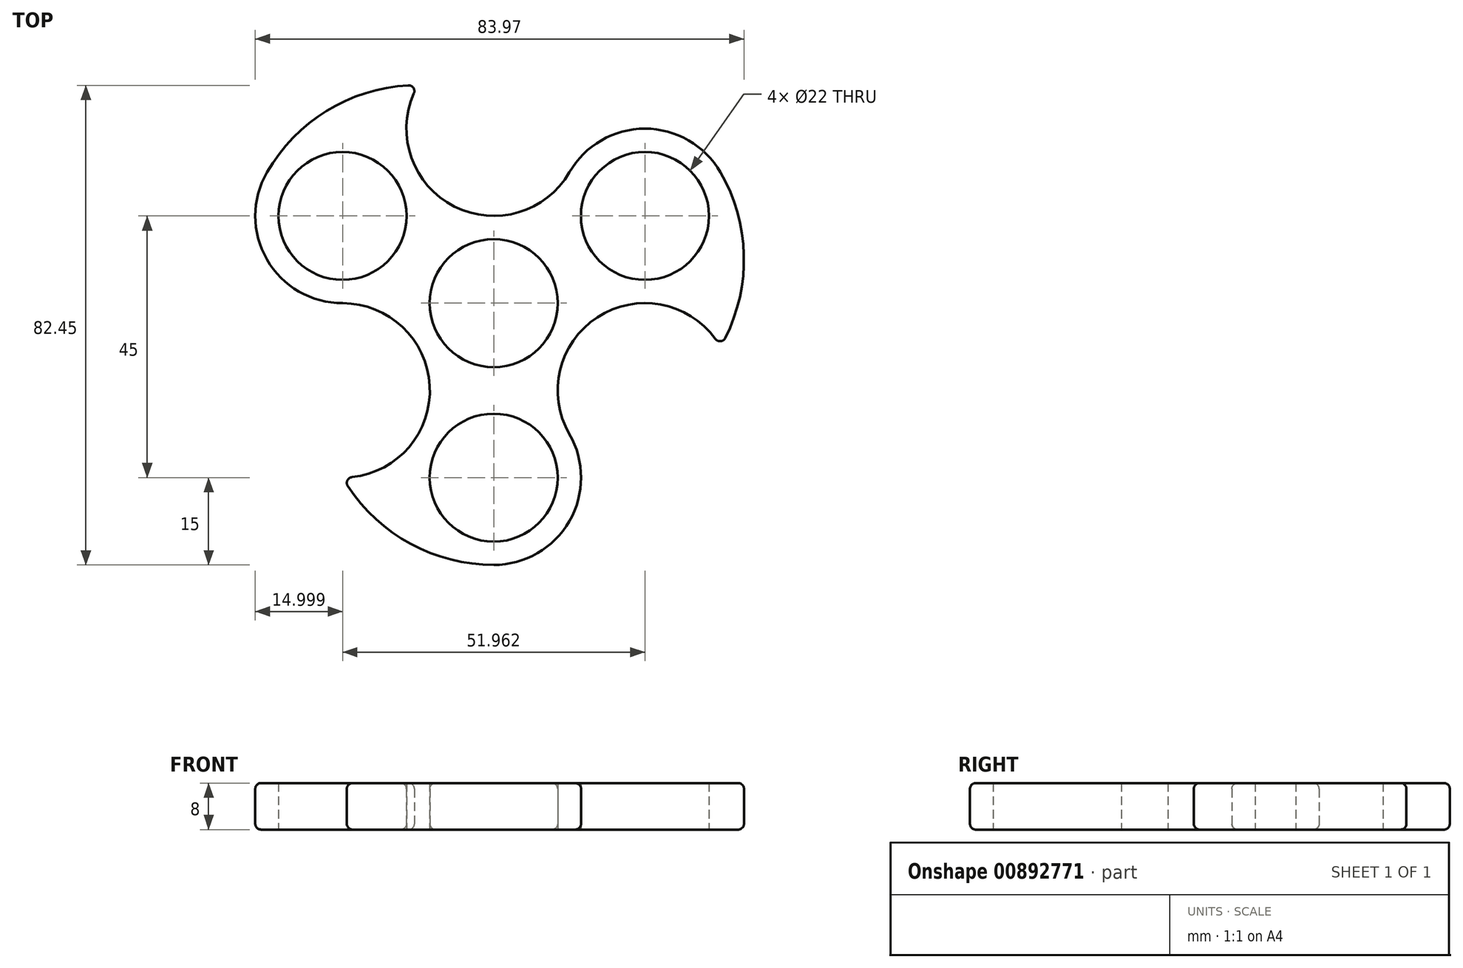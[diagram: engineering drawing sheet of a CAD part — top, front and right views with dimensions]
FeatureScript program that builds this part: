
annotation { "Feature Type Name" : "Feature", "Feature Type Description" : "" }
export const myFeature = defineFeature(function(context is Context, id is Id, definition is map)
    precondition{}
    {
        {
            var Q0;
            Q0=qCreatedBy(makeId("Top.planeOp"),FACE);
            var sketch = newSketch(context, id + "F0", { "sketchPlane" : qUnion([Q0])});
            skCircle(sketch, "E0", {"center": v(0, 0) * mm, "radius": 15 * mm});
            skCircle(sketch, "E1", {"center": v(-25.98, 15) * mm, "radius": 15 * mm});
            skCircle(sketch, "E2", {"center": v(0, -30) * mm, "radius": 15 * mm});
            skCircle(sketch, "E3", {"center": v(25.98, 15) * mm, "radius": 15 * mm});
            skLineSegment(sketch, "E4", {"start": v(-25.98, 15) * mm, "end": v(0, -30) * mm, "construction": true});
            skLineSegment(sketch, "E5", {"start": v(0, -30) * mm, "end": v(25.98, 15) * mm, "construction": true});
            skLineSegment(sketch, "E6", {"start": v(-25.98, 15) * mm, "end": v(25.98, 15) * mm, "construction": true});
            skArc(sketch, "E7", {"start": v(-13, -7.5) * mm, "mid": v(-18.48, -2) * mm, "end": v(-25.98, 0) * mm});
            skArc(sketch, "E8", {"start": v(-13, 22.5) * mm, "mid": v(-7.5, 17) * mm, "end": v(0, 15) * mm});
            skArc(sketch, "E9", {"start": v(25.98, 0) * mm, "mid": v(18.48, -2) * mm, "end": v(13, -7.5) * mm});
            skArc(sketch, "E10", {"start": v(0, 15) * mm, "mid": v(7.5, 17) * mm, "end": v(13, 22.5) * mm});
            skArc(sketch, "E11", {"start": v(-13, -22.5) * mm, "mid": v(-10.98, -15) * mm, "end": v(-13, -7.5) * mm});
            skArc(sketch, "E12", {"start": v(13, -7.5) * mm, "mid": v(10.98, -15) * mm, "end": v(13, -22.5) * mm});
            skArc(sketch, "E13", {"start": v(-25.08, -31.45) * mm, "mid": v(-14.25, -41.4) * mm, "end": v(0, -45) * mm});
            skArc(sketch, "E14", {"start": v(-24.36, -29.91) * mm, "mid": v(-17.79, -27.56) * mm, "end": v(-13, -22.5) * mm});
            skPoint(sketch, "E15.visualSharp", {"position": v(-25.98, -30) * mm});
            skArc(sketch, "E15.filletArc", {"start": v(-24.36, -29.91) * mm, "mid": v(-25.15, -30.48) * mm, "end": v(-25.08, -31.45) * mm});
            skArc(sketch, "E16.1.0", {"start": v(39.78, -6) * mm, "mid": v(42.98, 8.35) * mm, "end": v(38.97, 22.5) * mm});
            skArc(sketch, "E16.1.1", {"start": v(38.08, -6.14) * mm, "mid": v(32.77, -1.62) * mm, "end": v(25.98, 0) * mm});
            skArc(sketch, "E16.1.2", {"start": v(38.08, -6.14) * mm, "mid": v(38.97, -6.54) * mm, "end": v(39.78, -6) * mm});
            skArc(sketch, "E16.2.0", {"start": v(-14.7, 37.45) * mm, "mid": v(-28.72, 33.04) * mm, "end": v(-38.97, 22.5) * mm});
            skArc(sketch, "E16.2.1", {"start": v(-13.73, 36.05) * mm, "mid": v(-14.98, 29.19) * mm, "end": v(-13, 22.5) * mm});
            skArc(sketch, "E16.2.2", {"start": v(-13.73, 36.05) * mm, "mid": v(-13.82, 37.02) * mm, "end": v(-14.7, 37.45) * mm});
            skSolve(sketch);
        }
        {
            var Q0;
            {var subQ2=sQuery(id+"F0.wireOp",EDGE,"E16.2.0");Q0=makeQuery(id+"F0.imprint","IMPRINT",FACE,{"disambiguationData":[TD([[makeQuery(id+"F0.imprint","IMPRINT",EDGE,{"derivedFrom":subQ2}),1.0]])]});}
            var Q1;
            {var subQ0=sQuery(id+"F0.wireOp",EDGE,"E11");Q1=makeQuery(id+"F0.imprint","IMPRINT",FACE,{"disambiguationData":[TD([[makeQuery(id+"F0.imprint","IMPRINT",EDGE,{"derivedFrom":subQ0}),-1.0]])]});}
            var Q2;
            {var subQ2=sQuery(id+"F0.wireOp",EDGE,"E13");Q2=makeQuery(id+"F0.imprint","IMPRINT",FACE,{"disambiguationData":[TD([[makeQuery(id+"F0.imprint","IMPRINT",EDGE,{"derivedFrom":subQ2}),1.0]])]});}
            var Q3;
            {var subQ0=sQuery(id+"F0.wireOp",EDGE,"E12");Q3=makeQuery(id+"F0.imprint","IMPRINT",FACE,{"disambiguationData":[TD([[makeQuery(id+"F0.imprint","IMPRINT",EDGE,{"derivedFrom":subQ0}),-1.0]])]});}
            var Q4;
            {var subQ0=sQuery(id+"F0.wireOp",EDGE,"E7");Q4=makeQuery(id+"F0.imprint","IMPRINT",FACE,{"disambiguationData":[TD([[makeQuery(id+"F0.imprint","IMPRINT",EDGE,{"derivedFrom":subQ0}),-1.0]])]});}
            var Q5;
            {var subQ0=sQuery(id+"F0.wireOp",EDGE,"E0");var subQ5=makeQuery(id+"F0.imprint","INTERSECT",VERTEX,{"derivedFrom":[subQ0,sQuery(id+"F0.wireOp",EDGE,"E3")]});Q5=makeQuery(id+"F0.imprint","IMPRINT",FACE,{"disambiguationData":[TD([[makeQuery(id+"F0.imprint","IMPRINT",EDGE,{"disambiguationData":[TD([[subQ5,-1.0]])],"derivedFrom":subQ0}),1.0]])]});}
            var Q6;
            {var subQ0=sQuery(id+"F0.wireOp",EDGE,"E8");Q6=makeQuery(id+"F0.imprint","IMPRINT",FACE,{"disambiguationData":[TD([[makeQuery(id+"F0.imprint","IMPRINT",EDGE,{"derivedFrom":subQ0}),-1.0]])]});}
            var Q7;
            {var subQ0=sQuery(id+"F0.wireOp",EDGE,"E10");Q7=makeQuery(id+"F0.imprint","IMPRINT",FACE,{"disambiguationData":[TD([[makeQuery(id+"F0.imprint","IMPRINT",EDGE,{"derivedFrom":subQ0}),-1.0]])]});}
            var Q8;
            {var subQ0=sQuery(id+"F0.wireOp",EDGE,"E1");var subQ3=makeQuery(id+"F0.imprint","INTERSECT",VERTEX,{"derivedFrom":[subQ0,sQuery(id+"F0.wireOp",EDGE,"E7")]});Q8=makeQuery(id+"F0.imprint","IMPRINT",FACE,{"disambiguationData":[TD([[makeQuery(id+"F0.imprint","IMPRINT",EDGE,{"disambiguationData":[TD([[subQ3,1.0]])],"derivedFrom":subQ0}),1.0]])]});}
            var Q9;
            {var subQ2=sQuery(id+"F0.wireOp",EDGE,"E16.1.0");Q9=makeQuery(id+"F0.imprint","IMPRINT",FACE,{"disambiguationData":[TD([[makeQuery(id+"F0.imprint","IMPRINT",EDGE,{"derivedFrom":subQ2}),1.0]])]});}
            var Q10;
            {var subQ0=sQuery(id+"F0.wireOp",EDGE,"E3");var subQ1=makeQuery(id+"F0.imprint","INTERSECT",VERTEX,{"derivedFrom":[subQ0,sQuery(id+"F0.wireOp",EDGE,"E10")]});Q10=makeQuery(id+"F0.imprint","IMPRINT",FACE,{"disambiguationData":[TD([[makeQuery(id+"F0.imprint","IMPRINT",EDGE,{"disambiguationData":[TD([[subQ1,1.0]])],"derivedFrom":subQ0}),1.0]])]});}
            var Q11;
            {var subQ0=sQuery(id+"F0.wireOp",EDGE,"E2");var subQ1=makeQuery(id+"F0.imprint","INTERSECT",VERTEX,{"derivedFrom":[subQ0,sQuery(id+"F0.wireOp",EDGE,"E12")]});Q11=makeQuery(id+"F0.imprint","IMPRINT",FACE,{"disambiguationData":[TD([[makeQuery(id+"F0.imprint","IMPRINT",EDGE,{"disambiguationData":[TD([[subQ1,-1.0]])],"derivedFrom":subQ0}),1.0]])]});}
            var Q12;
            {var subQ0=sQuery(id+"F0.wireOp",EDGE,"E9");Q12=makeQuery(id+"F0.imprint","IMPRINT",FACE,{"disambiguationData":[TD([[makeQuery(id+"F0.imprint","IMPRINT",EDGE,{"derivedFrom":subQ0}),-1.0]])]});}
            extrude(context, id + "F1", {"entities" : qUnion([Q0, Q1, Q2, Q3, Q4, Q5, Q6, Q7, Q8, Q9, Q10, Q11, Q12]), "depth" : 8 * mm, "offsetDistance" : 25 * mm});
        }
        {
            var Q0;
            Q0=makeQuery(id+"F1.opExtrude","CAP_EDGE",EDGE,{"disambiguationData":[OSD([sQuery(id+"F0.wireOp",EDGE,"E1")])],"isStart":false});
            var Q1;
            Q1=makeQuery(id+"F1.opExtrude","SWEPT_FACE",FACE,{"disambiguationData":[OSD([sQuery(id+"F0.wireOp",EDGE,"E16.2.2")])]});
            var Q2;
            Q2=makeQuery(id+"F1.opExtrude","CAP_EDGE",EDGE,{"disambiguationData":[OSD([sQuery(id+"F0.wireOp",EDGE,"E2")])],"isStart":false});
            var Q3;
            Q3=makeQuery(id+"F1.opExtrude","SWEPT_FACE",FACE,{"disambiguationData":[OSD([sQuery(id+"F0.wireOp",EDGE,"E1")])]});
            var Q4;
            Q4=makeQuery(id+"F1.opExtrude","CAP_FACE",FACE,{"disambiguationData":[OSD([sQuery(id+"F0.wireOp",EDGE,"E1"),sQuery(id+"F0.wireOp",EDGE,"E2"),sQuery(id+"F0.wireOp",EDGE,"E3"),sQuery(id+"F0.wireOp",EDGE,"E7"),sQuery(id+"F0.wireOp",EDGE,"E8"),sQuery(id+"F0.wireOp",EDGE,"E9"),sQuery(id+"F0.wireOp",EDGE,"E10"),sQuery(id+"F0.wireOp",EDGE,"E11"),sQuery(id+"F0.wireOp",EDGE,"E12"),sQuery(id+"F0.wireOp",EDGE,"E13"),sQuery(id+"F0.wireOp",EDGE,"E14"),sQuery(id+"F0.wireOp",EDGE,"E15.filletArc"),sQuery(id+"F0.wireOp",EDGE,"E16.1.0"),sQuery(id+"F0.wireOp",EDGE,"E16.1.1"),sQuery(id+"F0.wireOp",EDGE,"E16.1.2"),sQuery(id+"F0.wireOp",EDGE,"E16.2.0"),sQuery(id+"F0.wireOp",EDGE,"E16.2.1"),sQuery(id+"F0.wireOp",EDGE,"E16.2.2")])],"isStart":false});
            var Q5;
            Q5=makeQuery(id+"F1.opExtrude","SWEPT_FACE",FACE,{"disambiguationData":[OSD([sQuery(id+"F0.wireOp",EDGE,"E2")])]});
            var Q6;
            Q6=makeQuery(id+"F1.opExtrude","SWEPT_FACE",FACE,{"disambiguationData":[OSD([sQuery(id+"F0.wireOp",EDGE,"E3")])]});
            var Q7;
            Q7=makeQuery(id+"F1.opExtrude","SWEPT_FACE",FACE,{"disambiguationData":[OSD([sQuery(id+"F0.wireOp",EDGE,"E7"),sQuery(id+"F0.wireOp",EDGE,"E11"),sQuery(id+"F0.wireOp",EDGE,"E14")])]});
            var Q8;
            Q8=makeQuery(id+"F1.opExtrude","SWEPT_FACE",FACE,{"disambiguationData":[OSD([sQuery(id+"F0.wireOp",EDGE,"E8"),sQuery(id+"F0.wireOp",EDGE,"E10"),sQuery(id+"F0.wireOp",EDGE,"E16.2.1")])]});
            var Q9;
            Q9=makeQuery(id+"F1.opExtrude","SWEPT_FACE",FACE,{"disambiguationData":[OSD([sQuery(id+"F0.wireOp",EDGE,"E9"),sQuery(id+"F0.wireOp",EDGE,"E12"),sQuery(id+"F0.wireOp",EDGE,"E16.1.1")])]});
            var Q10;
            Q10=makeQuery(id+"F1.opExtrude","SWEPT_FACE",FACE,{"disambiguationData":[OSD([sQuery(id+"F0.wireOp",EDGE,"E13")])]});
            var Q11;
            Q11=makeQuery(id+"F1.opExtrude","SWEPT_FACE",FACE,{"disambiguationData":[OSD([sQuery(id+"F0.wireOp",EDGE,"E15.filletArc")])]});
            var Q12;
            Q12=makeQuery(id+"F1.opExtrude","SWEPT_FACE",FACE,{"disambiguationData":[OSD([sQuery(id+"F0.wireOp",EDGE,"E16.1.0")])]});
            var Q13;
            Q13=makeQuery(id+"F1.opExtrude","SWEPT_FACE",FACE,{"disambiguationData":[OSD([sQuery(id+"F0.wireOp",EDGE,"E16.1.2")])]});
            var Q14;
            Q14=makeQuery(id+"F1.opExtrude","SWEPT_FACE",FACE,{"disambiguationData":[OSD([sQuery(id+"F0.wireOp",EDGE,"E16.2.0")])]});
            var Q15;
            Q15=makeQuery(id+"F1.opExtrude","CAP_EDGE",EDGE,{"disambiguationData":[OSD([sQuery(id+"F0.wireOp",EDGE,"E16.1.0")])],"isStart":false});
            var Q16;
            Q16=makeQuery(id+"F1.opExtrude","CAP_EDGE",EDGE,{"disambiguationData":[OSD([sQuery(id+"F0.wireOp",EDGE,"E3")])],"isStart":false});
            var Q17;
            Q17=makeQuery(id+"F1.opExtrude","CAP_EDGE",EDGE,{"disambiguationData":[OSD([sQuery(id+"F0.wireOp",EDGE,"E16.2.0")])],"isStart":false});
            var Q18;
            Q18=makeQuery(id+"F1.opExtrude","CAP_EDGE",EDGE,{"disambiguationData":[OSD([sQuery(id+"F0.wireOp",EDGE,"E7"),sQuery(id+"F0.wireOp",EDGE,"E11"),sQuery(id+"F0.wireOp",EDGE,"E14")])],"isStart":false});
            var Q19;
            Q19=makeQuery(id+"F1.opExtrude","CAP_EDGE",EDGE,{"disambiguationData":[OSD([sQuery(id+"F0.wireOp",EDGE,"E8"),sQuery(id+"F0.wireOp",EDGE,"E10"),sQuery(id+"F0.wireOp",EDGE,"E16.2.1")])],"isStart":false});
            var Q20;
            Q20=makeQuery(id+"F1.opExtrude","CAP_EDGE",EDGE,{"disambiguationData":[OSD([sQuery(id+"F0.wireOp",EDGE,"E9"),sQuery(id+"F0.wireOp",EDGE,"E12"),sQuery(id+"F0.wireOp",EDGE,"E16.1.1")])],"isStart":false});
            var Q21;
            Q21=makeQuery(id+"F1.opExtrude","CAP_EDGE",EDGE,{"disambiguationData":[OSD([sQuery(id+"F0.wireOp",EDGE,"E13")])],"isStart":false});
            var Q22;
            Q22=makeQuery(id+"F1.opExtrude","CAP_EDGE",EDGE,{"disambiguationData":[OSD([sQuery(id+"F0.wireOp",EDGE,"E2")])],"isStart":true});
            var Q23;
            Q23=makeQuery(id+"F1.opExtrude","SWEPT_EDGE",EDGE,{"disambiguationData":[OSD([sQuery(id+"F0.wireOp",EDGE,"E1"),sQuery(id+"F0.wireOp",EDGE,"E7")])]});
            var Q24;
            Q24=makeQuery(id+"F1.opExtrude","SWEPT_EDGE",EDGE,{"disambiguationData":[OSD([sQuery(id+"F0.wireOp",EDGE,"E3"),sQuery(id+"F0.wireOp",EDGE,"E10")])]});
            var Q25;
            Q25=makeQuery(id+"F1.opExtrude","CAP_FACE",FACE,{"disambiguationData":[OSD([sQuery(id+"F0.wireOp",EDGE,"E1"),sQuery(id+"F0.wireOp",EDGE,"E2"),sQuery(id+"F0.wireOp",EDGE,"E3"),sQuery(id+"F0.wireOp",EDGE,"E7"),sQuery(id+"F0.wireOp",EDGE,"E8"),sQuery(id+"F0.wireOp",EDGE,"E9"),sQuery(id+"F0.wireOp",EDGE,"E10"),sQuery(id+"F0.wireOp",EDGE,"E11"),sQuery(id+"F0.wireOp",EDGE,"E12"),sQuery(id+"F0.wireOp",EDGE,"E13"),sQuery(id+"F0.wireOp",EDGE,"E14"),sQuery(id+"F0.wireOp",EDGE,"E15.filletArc"),sQuery(id+"F0.wireOp",EDGE,"E16.1.0"),sQuery(id+"F0.wireOp",EDGE,"E16.1.1"),sQuery(id+"F0.wireOp",EDGE,"E16.1.2"),sQuery(id+"F0.wireOp",EDGE,"E16.2.0"),sQuery(id+"F0.wireOp",EDGE,"E16.2.1"),sQuery(id+"F0.wireOp",EDGE,"E16.2.2")])],"isStart":true});
            var Q26;
            Q26=makeQuery(id+"F1.opExtrude","SWEPT_EDGE",EDGE,{"disambiguationData":[OSD([sQuery(id+"F0.wireOp",EDGE,"E2"),sQuery(id+"F0.wireOp",EDGE,"E12")])]});
            var Q27;
            Q27=makeQuery(id+"F1.opExtrude","SWEPT_EDGE",EDGE,{"disambiguationData":[OSD([sQuery(id+"F0.wireOp",EDGE,"E13"),sQuery(id+"F0.wireOp",EDGE,"E15.filletArc")])]});
            var Q28;
            Q28=makeQuery(id+"F1.opExtrude","SWEPT_EDGE",EDGE,{"disambiguationData":[OSD([sQuery(id+"F0.wireOp",EDGE,"E2"),sQuery(id+"F0.wireOp",EDGE,"E13")])]});
            var Q29;
            Q29=makeQuery(id+"F1.opExtrude","SWEPT_EDGE",EDGE,{"disambiguationData":[OSD([sQuery(id+"F0.wireOp",EDGE,"E14"),sQuery(id+"F0.wireOp",EDGE,"E15.filletArc")])]});
            var Q30;
            Q30=makeQuery(id+"F1.opExtrude","SWEPT_EDGE",EDGE,{"disambiguationData":[OSD([sQuery(id+"F0.wireOp",EDGE,"E16.1.0"),sQuery(id+"F0.wireOp",EDGE,"E16.1.2")])]});
            var Q31;
            Q31=makeQuery(id+"F1.opExtrude","SWEPT_EDGE",EDGE,{"disambiguationData":[OSD([sQuery(id+"F0.wireOp",EDGE,"E3"),sQuery(id+"F0.wireOp",EDGE,"E16.1.0")])]});
            var Q32;
            Q32=makeQuery(id+"F1.opExtrude","SWEPT_EDGE",EDGE,{"disambiguationData":[OSD([sQuery(id+"F0.wireOp",EDGE,"E16.1.1"),sQuery(id+"F0.wireOp",EDGE,"E16.1.2")])]});
            var Q33;
            Q33=makeQuery(id+"F1.opExtrude","SWEPT_EDGE",EDGE,{"disambiguationData":[OSD([sQuery(id+"F0.wireOp",EDGE,"E16.2.0"),sQuery(id+"F0.wireOp",EDGE,"E16.2.2")])]});
            var Q34;
            Q34=makeQuery(id+"F1.opExtrude","SWEPT_EDGE",EDGE,{"disambiguationData":[OSD([sQuery(id+"F0.wireOp",EDGE,"E1"),sQuery(id+"F0.wireOp",EDGE,"E16.2.0")])]});
            var Q35;
            Q35=makeQuery(id+"F1.opExtrude","SWEPT_EDGE",EDGE,{"disambiguationData":[OSD([sQuery(id+"F0.wireOp",EDGE,"E16.2.1"),sQuery(id+"F0.wireOp",EDGE,"E16.2.2")])]});
            var Q36;
            Q36=makeQuery(id+"F1.opExtrude","CAP_EDGE",EDGE,{"disambiguationData":[OSD([sQuery(id+"F0.wireOp",EDGE,"E1")])],"isStart":true});
            var Q37;
            Q37=makeQuery(id+"F1.opExtrude","CAP_EDGE",EDGE,{"disambiguationData":[OSD([sQuery(id+"F0.wireOp",EDGE,"E16.1.2")])],"isStart":false});
            var Q38;
            Q38=makeQuery(id+"F1.opExtrude","CAP_EDGE",EDGE,{"disambiguationData":[OSD([sQuery(id+"F0.wireOp",EDGE,"E3")])],"isStart":true});
            var Q39;
            Q39=makeQuery(id+"F1.opExtrude","CAP_EDGE",EDGE,{"disambiguationData":[OSD([sQuery(id+"F0.wireOp",EDGE,"E16.2.0")])],"isStart":true});
            var Q40;
            Q40=makeQuery(id+"F1.opExtrude","CAP_EDGE",EDGE,{"disambiguationData":[OSD([sQuery(id+"F0.wireOp",EDGE,"E7"),sQuery(id+"F0.wireOp",EDGE,"E11"),sQuery(id+"F0.wireOp",EDGE,"E14")])],"isStart":true});
            var Q41;
            Q41=makeQuery(id+"F1.opExtrude","CAP_EDGE",EDGE,{"disambiguationData":[OSD([sQuery(id+"F0.wireOp",EDGE,"E16.2.2")])],"isStart":false});
            var Q42;
            Q42=makeQuery(id+"F1.opExtrude","CAP_EDGE",EDGE,{"disambiguationData":[OSD([sQuery(id+"F0.wireOp",EDGE,"E8"),sQuery(id+"F0.wireOp",EDGE,"E10"),sQuery(id+"F0.wireOp",EDGE,"E16.2.1")])],"isStart":true});
            var Q43;
            Q43=makeQuery(id+"F1.opExtrude","CAP_EDGE",EDGE,{"disambiguationData":[OSD([sQuery(id+"F0.wireOp",EDGE,"E9"),sQuery(id+"F0.wireOp",EDGE,"E12"),sQuery(id+"F0.wireOp",EDGE,"E16.1.1")])],"isStart":true});
            var Q44;
            Q44=makeQuery(id+"F1.opExtrude","CAP_EDGE",EDGE,{"disambiguationData":[OSD([sQuery(id+"F0.wireOp",EDGE,"E13")])],"isStart":true});
            var Q45;
            Q45=makeQuery(id+"F1.opExtrude","CAP_EDGE",EDGE,{"disambiguationData":[OSD([sQuery(id+"F0.wireOp",EDGE,"E15.filletArc")])],"isStart":false});
            var Q46;
            Q46=makeQuery(id+"F1.opExtrude","CAP_EDGE",EDGE,{"disambiguationData":[OSD([sQuery(id+"F0.wireOp",EDGE,"E16.1.0")])],"isStart":true});
            var Q47;
            Q47=makeQuery(id+"F1.opExtrude","CAP_EDGE",EDGE,{"disambiguationData":[OSD([sQuery(id+"F0.wireOp",EDGE,"E16.1.2")])],"isStart":true});
            var Q48;
            Q48=makeQuery(id+"F1.opExtrude","CAP_EDGE",EDGE,{"disambiguationData":[OSD([sQuery(id+"F0.wireOp",EDGE,"E16.2.2")])],"isStart":true});
            var Q49;
            Q49=makeQuery(id+"F1.opExtrude","CAP_EDGE",EDGE,{"disambiguationData":[OSD([sQuery(id+"F0.wireOp",EDGE,"E15.filletArc")])],"isStart":true});
            fillet(context, id + "F2", {"entities" : qUnion([Q0, Q1, Q2, Q3, Q4, Q5, Q6, Q7, Q8, Q9, Q10, Q11, Q12, Q13, Q14, Q15, Q16, Q17, Q18, Q19, Q20, Q21, Q22, Q23, Q24, Q25, Q26, Q27, Q28, Q29, Q30, Q31, Q32, Q33, Q34, Q35, Q36, Q37, Q38, Q39, Q40, Q41, Q42, Q43, Q44, Q45, Q46, Q47, Q48, Q49]), "radius" : 1 * mm, "tangentPropagation" : true, "allowEdgeOverflow" : false});
        }
        {
            var Q0;
            Q0=sQuery(id+"F0.wireOp",VERTEX,"E4.start");
            var Q1;
            Q1=sQuery(id+"F0.wireOp",VERTEX,"E5.end");
            var Q2;
            Q2=sQuery(id+"F0.wireOp",VERTEX,"E0.center");
            var Q3;
            Q3=sQuery(id+"F0.wireOp",VERTEX,"E4.end");
            var Q4;
            Q4=makeQuery(id+"F1.opExtrude","SWEPT_BODY",BODY,{"disambiguationData":[OSD([sQuery(id+"F0.wireOp",EDGE,"E1"),sQuery(id+"F0.wireOp",EDGE,"E2"),sQuery(id+"F0.wireOp",EDGE,"E3"),sQuery(id+"F0.wireOp",EDGE,"E7"),sQuery(id+"F0.wireOp",EDGE,"E8"),sQuery(id+"F0.wireOp",EDGE,"E9"),sQuery(id+"F0.wireOp",EDGE,"E10"),sQuery(id+"F0.wireOp",EDGE,"E11"),sQuery(id+"F0.wireOp",EDGE,"E12"),sQuery(id+"F0.wireOp",EDGE,"E13"),sQuery(id+"F0.wireOp",EDGE,"E14"),sQuery(id+"F0.wireOp",EDGE,"E15.filletArc"),sQuery(id+"F0.wireOp",EDGE,"E16.1.0"),sQuery(id+"F0.wireOp",EDGE,"E16.1.1"),sQuery(id+"F0.wireOp",EDGE,"E16.1.2"),sQuery(id+"F0.wireOp",EDGE,"E16.2.0"),sQuery(id+"F0.wireOp",EDGE,"E16.2.1"),sQuery(id+"F0.wireOp",EDGE,"E16.2.2")])]});
            hole(context, id + "F3", {"style" : HoleStyle.SIMPLE, "endStyle" : HoleEndStyle.THROUGH, "oppositeDirection" : true, "holeDiameter" : 22 * mm, "majorDiameter" : 5 * mm, "isTappedThrough" : true, "tappedDepth" : 12 * mm, "tapClearance" : 3, "locations" : qUnion([Q0, Q1, Q2, Q3]), "scope" : qUnion([Q4])});
        }
    });
